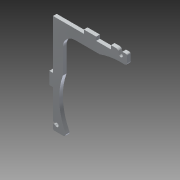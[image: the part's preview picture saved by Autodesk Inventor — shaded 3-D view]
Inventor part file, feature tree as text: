
AUTODESK INVENTOR PART (.ipt)
format: ipt  version: 2015 (Build 190159000, 159)  size: 166,912 bytes
history: native  units: mm
features: extrude x1, sketch x1
ambient origin geometry x8: Origin, YZ Plane, XZ Plane, XY Plane, X Axis, Y Axis, Z Axis, Center Point
bodies: Body1 (feature_tree)
feature tree (2):
  extrude  "Extrusion3"  Depth=10.0mm
  sketch  "Sketch2"  dims[d0=100.0mm d5=10.0mm d6=10.0mm d13=40.0mm d14=25.0mm d15=3.0mm d16=3.0mm d17=3.0mm d18=3.0mm d22=55.0mm d23=55.0mm d31=3.0mm d33=135.0deg d34=45.0deg d35=135.0deg d36=45.0deg d37=3.0mm d43=12.0mm d44=3.0mm d46=3.0mm d48=3.0mm d50=45.0deg d51=135.0deg d53=2.0mm d54=1.0mm d57=80.0mm d58=3.0mm d59=5.0mm d60=3.0mm d61=3.0mm d62=135.0deg d63=45.0deg d64=1.0mm d65=2.0mm d66=1.0mm d67=3.0mm d75=4.050253mm d76=60.0mm d78=5.0mm d79=3.0mm d85=3.0mm d86=0.0mm d87=60.0deg d92=8.0mm d93=50.0mm d94=50.0mm d95=8.0mm d96=10.0mm d97=2.0mm d98=2.0mm]
